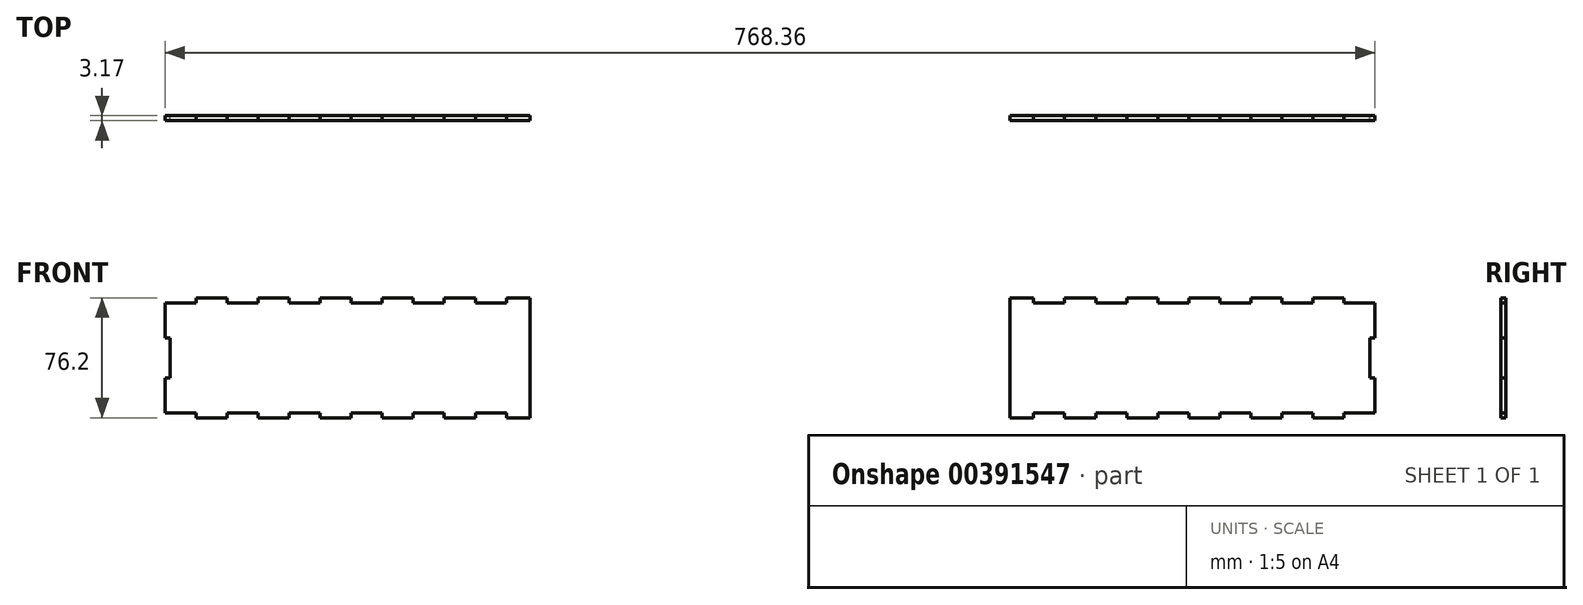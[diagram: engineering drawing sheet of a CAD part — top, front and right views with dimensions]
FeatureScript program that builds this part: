
annotation { "Feature Type Name" : "Feature", "Feature Type Description" : "" }
export const myFeature = defineFeature(function(context is Context, id is Id, definition is map)
    precondition{}
    {
        {
            var Q0;
            Q0=qCreatedBy(makeId("Front.planeOp"),FACE);
            var sketch = newSketch(context, id + "F0", { "sketchPlane" : qUnion([Q0])});
            skLineSegment(sketch, "E0.bottom", {"start": v(-384.18, -38.1) * mm, "end": v(384.17, -38.1) * mm, "construction": true});
            skLineSegment(sketch, "E0.left", {"start": v(-384.18, -38.1) * mm, "end": v(-384.18, 38.1) * mm, "construction": true});
            skPoint(sketch, "E0.middle", {"position": v(0, 0) * mm});
            skLineSegment(sketch, "E1", {"start": v(-384.18, 12.7) * mm, "end": v(-381, 12.7) * mm});
            skLineSegment(sketch, "E2", {"start": v(-381, 12.7) * mm, "end": v(-381, -12.7) * mm});
            skLineSegment(sketch, "E3", {"start": v(-381, -12.7) * mm, "end": v(-384.18, -12.7) * mm});
            skLineSegment(sketch, "E4", {"start": v(-384.18, -12.7) * mm, "end": v(-384.18, -38.1) * mm});
            skLineSegment(sketch, "E5", {"start": v(-384.18, 34.92) * mm, "end": v(-364.47, 34.92) * mm});
            skLineSegment(sketch, "E6", {"start": v(-364.47, 34.92) * mm, "end": v(-364.47, 38.1) * mm});
            skLineSegment(sketch, "E7", {"start": v(-364.47, 38.1) * mm, "end": v(-344.77, 38.1) * mm});
            skLineSegment(sketch, "E8", {"start": v(-344.77, 38.1) * mm, "end": v(-344.77, 34.93) * mm});
            skLineSegment(sketch, "E9", {"start": v(-384.18, 38.1) * mm, "end": v(384.17, 38.1) * mm, "construction": true});
            skLineSegment(sketch, "E10.1.0.0", {"start": v(-344.77, 34.92) * mm, "end": v(-325.07, 34.92) * mm});
            skLineSegment(sketch, "E10.1.0.1", {"start": v(-325.07, 34.92) * mm, "end": v(-325.07, 38.1) * mm});
            skLineSegment(sketch, "E10.1.0.2", {"start": v(-325.07, 38.1) * mm, "end": v(-305.37, 38.1) * mm});
            skLineSegment(sketch, "E10.1.0.3", {"start": v(-305.37, 38.1) * mm, "end": v(-305.37, 34.93) * mm});
            skLineSegment(sketch, "E10.2.0.0", {"start": v(-305.37, 34.92) * mm, "end": v(-285.67, 34.92) * mm});
            skLineSegment(sketch, "E10.2.0.1", {"start": v(-285.67, 34.92) * mm, "end": v(-285.67, 38.1) * mm});
            skLineSegment(sketch, "E10.2.0.2", {"start": v(-285.67, 38.1) * mm, "end": v(-265.97, 38.1) * mm});
            skLineSegment(sketch, "E10.2.0.3", {"start": v(-265.97, 38.1) * mm, "end": v(-265.97, 34.93) * mm});
            skLineSegment(sketch, "E10.3.0.0", {"start": v(-265.97, 34.92) * mm, "end": v(-246.27, 34.92) * mm});
            skLineSegment(sketch, "E10.3.0.1", {"start": v(-246.27, 34.92) * mm, "end": v(-246.27, 38.1) * mm});
            skLineSegment(sketch, "E10.3.0.2", {"start": v(-246.27, 38.1) * mm, "end": v(-226.56, 38.1) * mm});
            skLineSegment(sketch, "E10.3.0.3", {"start": v(-226.56, 38.1) * mm, "end": v(-226.56, 34.93) * mm});
            skLineSegment(sketch, "E10.4.0.0", {"start": v(-226.56, 34.92) * mm, "end": v(-206.86, 34.92) * mm});
            skLineSegment(sketch, "E10.4.0.1", {"start": v(-206.86, 34.92) * mm, "end": v(-206.86, 38.1) * mm});
            skLineSegment(sketch, "E10.4.0.2", {"start": v(-206.86, 38.1) * mm, "end": v(-187.16, 38.1) * mm});
            skLineSegment(sketch, "E10.4.0.3", {"start": v(-187.16, 38.1) * mm, "end": v(-187.16, 34.93) * mm});
            skLineSegment(sketch, "E10.5.0.0", {"start": v(-187.16, 34.92) * mm, "end": v(-167.46, 34.92) * mm});
            skLineSegment(sketch, "E10.5.0.1", {"start": v(-167.46, 34.92) * mm, "end": v(-167.46, 38.1) * mm});
            skLineSegment(sketch, "E10.5.0.2", {"start": v(-167.46, 38.1) * mm, "end": v(-147.76, 38.1) * mm});
            skLineSegment(sketch, "E10.5.0.3", {"start": v(-147.76, 38.1) * mm, "end": v(-147.76, 34.93) * mm});
            skLineSegment(sketch, "E10.6.0.0", {"start": v(-147.76, 34.92) * mm, "end": v(-128.06, 34.92) * mm});
            skLineSegment(sketch, "E10.6.0.1", {"start": v(-128.06, 34.92) * mm, "end": v(-128.06, 38.1) * mm});
            skLineSegment(sketch, "E10.6.0.2", {"start": v(-128.06, 38.1) * mm, "end": v(-108.36, 38.1) * mm});
            skLineSegment(sketch, "E10.6.0.3", {"start": v(-108.36, 38.1) * mm, "end": v(-108.36, 34.93) * mm});
            skLineSegment(sketch, "E10.7.0.0", {"start": v(-108.36, 34.92) * mm, "end": v(-88.66, 34.92) * mm});
            skLineSegment(sketch, "E10.7.0.1", {"start": v(-88.66, 34.92) * mm, "end": v(-88.66, 38.1) * mm});
            skLineSegment(sketch, "E10.7.0.2", {"start": v(-88.66, 38.1) * mm, "end": v(-68.95, 38.1) * mm});
            skLineSegment(sketch, "E10.7.0.3", {"start": v(-68.95, 38.1) * mm, "end": v(-68.95, 34.93) * mm});
            skLineSegment(sketch, "E10.8.0.0", {"start": v(-68.95, 34.92) * mm, "end": v(-49.25, 34.92) * mm});
            skLineSegment(sketch, "E10.8.0.1", {"start": v(-49.25, 34.92) * mm, "end": v(-49.25, 38.1) * mm});
            skLineSegment(sketch, "E10.8.0.2", {"start": v(-49.25, 38.1) * mm, "end": v(-29.55, 38.1) * mm});
            skLineSegment(sketch, "E10.8.0.3", {"start": v(-29.55, 38.1) * mm, "end": v(-29.55, 34.93) * mm});
            skLineSegment(sketch, "E10.9.0.0", {"start": v(-29.55, 34.92) * mm, "end": v(-9.85, 34.92) * mm});
            skLineSegment(sketch, "E10.9.0.1", {"start": v(-9.85, 34.92) * mm, "end": v(-9.85, 38.1) * mm});
            skLineSegment(sketch, "E10.9.0.2", {"start": v(-9.85, 38.1) * mm, "end": v(9.85, 38.1) * mm});
            skLineSegment(sketch, "E10.9.0.3", {"start": v(9.85, 38.1) * mm, "end": v(9.85, 34.93) * mm});
            skLineSegment(sketch, "E10.10.0.0", {"start": v(9.85, 34.92) * mm, "end": v(29.55, 34.92) * mm});
            skLineSegment(sketch, "E10.10.0.1", {"start": v(29.55, 34.92) * mm, "end": v(29.55, 38.1) * mm});
            skLineSegment(sketch, "E10.10.0.2", {"start": v(29.55, 38.1) * mm, "end": v(49.25, 38.1) * mm});
            skLineSegment(sketch, "E10.10.0.3", {"start": v(49.25, 38.1) * mm, "end": v(49.25, 34.93) * mm});
            skLineSegment(sketch, "E10.11.0.0", {"start": v(49.25, 34.92) * mm, "end": v(68.95, 34.92) * mm});
            skLineSegment(sketch, "E10.11.0.1", {"start": v(68.95, 34.92) * mm, "end": v(68.95, 38.1) * mm});
            skLineSegment(sketch, "E10.11.0.2", {"start": v(68.95, 38.1) * mm, "end": v(88.66, 38.1) * mm});
            skLineSegment(sketch, "E10.11.0.3", {"start": v(88.66, 38.1) * mm, "end": v(88.66, 34.93) * mm});
            skLineSegment(sketch, "E10.12.0.0", {"start": v(88.66, 34.92) * mm, "end": v(108.36, 34.92) * mm});
            skLineSegment(sketch, "E10.12.0.1", {"start": v(108.36, 34.92) * mm, "end": v(108.36, 38.1) * mm});
            skLineSegment(sketch, "E10.12.0.2", {"start": v(108.36, 38.1) * mm, "end": v(128.06, 38.1) * mm});
            skLineSegment(sketch, "E10.12.0.3", {"start": v(128.06, 38.1) * mm, "end": v(128.06, 34.93) * mm});
            skLineSegment(sketch, "E10.13.0.0", {"start": v(128.06, 34.92) * mm, "end": v(147.76, 34.92) * mm});
            skLineSegment(sketch, "E10.13.0.1", {"start": v(147.76, 34.92) * mm, "end": v(147.76, 38.1) * mm});
            skLineSegment(sketch, "E10.13.0.2", {"start": v(147.76, 38.1) * mm, "end": v(167.46, 38.1) * mm});
            skLineSegment(sketch, "E10.13.0.3", {"start": v(167.46, 38.1) * mm, "end": v(167.46, 34.93) * mm});
            skLineSegment(sketch, "E10.14.0.0", {"start": v(167.46, 34.92) * mm, "end": v(187.16, 34.92) * mm});
            skLineSegment(sketch, "E10.14.0.1", {"start": v(187.16, 34.92) * mm, "end": v(187.16, 38.1) * mm});
            skLineSegment(sketch, "E10.14.0.2", {"start": v(187.16, 38.1) * mm, "end": v(206.86, 38.1) * mm});
            skLineSegment(sketch, "E10.14.0.3", {"start": v(206.86, 38.1) * mm, "end": v(206.86, 34.93) * mm});
            skLineSegment(sketch, "E10.15.0.0", {"start": v(206.86, 34.92) * mm, "end": v(226.56, 34.92) * mm});
            skLineSegment(sketch, "E10.15.0.1", {"start": v(226.56, 34.92) * mm, "end": v(226.56, 38.1) * mm});
            skLineSegment(sketch, "E10.15.0.2", {"start": v(226.56, 38.1) * mm, "end": v(246.27, 38.1) * mm});
            skLineSegment(sketch, "E10.15.0.3", {"start": v(246.27, 38.1) * mm, "end": v(246.27, 34.93) * mm});
            skLineSegment(sketch, "E10.16.0.0", {"start": v(246.27, 34.92) * mm, "end": v(265.97, 34.92) * mm});
            skLineSegment(sketch, "E10.16.0.1", {"start": v(265.97, 34.92) * mm, "end": v(265.97, 38.1) * mm});
            skLineSegment(sketch, "E10.16.0.2", {"start": v(265.97, 38.1) * mm, "end": v(285.67, 38.1) * mm});
            skLineSegment(sketch, "E10.16.0.3", {"start": v(285.67, 38.1) * mm, "end": v(285.67, 34.93) * mm});
            skLineSegment(sketch, "E10.17.0.0", {"start": v(285.67, 34.92) * mm, "end": v(305.37, 34.92) * mm});
            skLineSegment(sketch, "E10.17.0.1", {"start": v(305.37, 34.92) * mm, "end": v(305.37, 38.1) * mm});
            skLineSegment(sketch, "E10.17.0.2", {"start": v(305.37, 38.1) * mm, "end": v(325.07, 38.1) * mm});
            skLineSegment(sketch, "E10.17.0.3", {"start": v(325.07, 38.1) * mm, "end": v(325.07, 34.93) * mm});
            skLineSegment(sketch, "E10.18.0.0", {"start": v(325.07, 34.92) * mm, "end": v(344.77, 34.92) * mm});
            skLineSegment(sketch, "E10.18.0.1", {"start": v(344.77, 34.92) * mm, "end": v(344.77, 38.1) * mm});
            skLineSegment(sketch, "E10.18.0.2", {"start": v(344.77, 38.1) * mm, "end": v(364.47, 38.1) * mm});
            skLineSegment(sketch, "E10.18.0.3", {"start": v(364.47, 38.1) * mm, "end": v(364.47, 34.93) * mm});
            skLineSegment(sketch, "E10.19.0.0", {"start": v(364.47, 34.92) * mm, "end": v(384.18, 34.92) * mm});
            skLineSegment(sketch, "E10.direction1", {"start": v(-384.18, 34.92) * mm, "end": v(-344.77, 34.92) * mm, "construction": true});
            skLineSegment(sketch, "E11", {"start": v(-384.18, 34.92) * mm, "end": v(-384.18, 12.7) * mm});
            skLineSegment(sketch, "E12.MirrorCS", {"start": v(-364.47, -34.92) * mm, "end": v(-364.47, -38.1) * mm});
            skLineSegment(sketch, "E13.MirrorCS", {"start": v(-265.97, -38.1) * mm, "end": v(-265.97, -34.93) * mm});
            skLineSegment(sketch, "E14.MirrorCS", {"start": v(364.47, -38.1) * mm, "end": v(364.47, -34.93) * mm});
            skLineSegment(sketch, "E15.MirrorCS", {"start": v(206.86, -38.1) * mm, "end": v(206.86, -34.93) * mm});
            skLineSegment(sketch, "E16.MirrorCS", {"start": v(49.25, -38.1) * mm, "end": v(49.25, -34.93) * mm});
            skLineSegment(sketch, "E17.MirrorCS", {"start": v(-108.36, -38.1) * mm, "end": v(-108.36, -34.93) * mm});
            skLineSegment(sketch, "E18.MirrorCS", {"start": v(-325.07, -34.92) * mm, "end": v(-325.07, -38.1) * mm});
            skLineSegment(sketch, "E19.MirrorCS", {"start": v(-344.77, -38.1) * mm, "end": v(-344.77, -34.93) * mm});
            skLineSegment(sketch, "E20.MirrorCS", {"start": v(128.06, -38.1) * mm, "end": v(128.06, -34.93) * mm});
            skLineSegment(sketch, "E21.MirrorCS", {"start": v(-29.55, -38.1) * mm, "end": v(-29.55, -34.93) * mm});
            skLineSegment(sketch, "E22.MirrorCS", {"start": v(-187.16, -38.1) * mm, "end": v(-187.16, -34.93) * mm});
            skLineSegment(sketch, "E23.MirrorCS", {"start": v(285.67, -38.1) * mm, "end": v(285.67, -34.93) * mm});
            skLineSegment(sketch, "E24.MirrorCS", {"start": v(305.37, -34.92) * mm, "end": v(305.37, -38.1) * mm});
            skLineSegment(sketch, "E25.MirrorCS", {"start": v(147.76, -34.92) * mm, "end": v(147.76, -38.1) * mm});
            skLineSegment(sketch, "E26.MirrorCS", {"start": v(-9.85, -34.92) * mm, "end": v(-9.85, -38.1) * mm});
            skLineSegment(sketch, "E27.MirrorCS", {"start": v(-167.46, -34.92) * mm, "end": v(-167.46, -38.1) * mm});
            skLineSegment(sketch, "E28.MirrorCS", {"start": v(-246.27, -34.92) * mm, "end": v(-246.27, -38.1) * mm});
            skLineSegment(sketch, "E29.MirrorCS", {"start": v(226.56, -34.92) * mm, "end": v(226.56, -38.1) * mm});
            skLineSegment(sketch, "E30.MirrorCS", {"start": v(68.95, -34.92) * mm, "end": v(68.95, -38.1) * mm});
            skLineSegment(sketch, "E31.MirrorCS", {"start": v(-88.66, -34.92) * mm, "end": v(-88.66, -38.1) * mm});
            skLineSegment(sketch, "E32.MirrorCS", {"start": v(-305.37, -38.1) * mm, "end": v(-305.37, -34.93) * mm});
            skLineSegment(sketch, "E33.MirrorCS", {"start": v(88.66, -38.1) * mm, "end": v(88.66, -34.93) * mm});
            skLineSegment(sketch, "E34.MirrorCS", {"start": v(-68.95, -38.1) * mm, "end": v(-68.95, -34.93) * mm});
            skLineSegment(sketch, "E35.MirrorCS", {"start": v(-226.56, -38.1) * mm, "end": v(-226.56, -34.93) * mm});
            skLineSegment(sketch, "E36.MirrorCS", {"start": v(246.27, -38.1) * mm, "end": v(246.27, -34.93) * mm});
            skLineSegment(sketch, "E37.MirrorCS", {"start": v(-285.67, -34.92) * mm, "end": v(-285.67, -38.1) * mm});
            skLineSegment(sketch, "E38.MirrorCS", {"start": v(344.77, -34.92) * mm, "end": v(344.77, -38.1) * mm});
            skLineSegment(sketch, "E39.MirrorCS", {"start": v(187.16, -34.92) * mm, "end": v(187.16, -38.1) * mm});
            skLineSegment(sketch, "E40.MirrorCS", {"start": v(29.55, -34.92) * mm, "end": v(29.55, -38.1) * mm});
            skLineSegment(sketch, "E41.MirrorCS", {"start": v(-128.06, -34.92) * mm, "end": v(-128.06, -38.1) * mm});
            skLineSegment(sketch, "E42.MirrorCS", {"start": v(-49.25, -34.92) * mm, "end": v(-49.25, -38.1) * mm});
            skLineSegment(sketch, "E43.MirrorCS", {"start": v(108.36, -34.92) * mm, "end": v(108.36, -38.1) * mm});
            skLineSegment(sketch, "E44.MirrorCS", {"start": v(-206.86, -34.92) * mm, "end": v(-206.86, -38.1) * mm});
            skLineSegment(sketch, "E45.MirrorCS", {"start": v(265.97, -34.92) * mm, "end": v(265.97, -38.1) * mm});
            skLineSegment(sketch, "E46.MirrorCS", {"start": v(325.07, -38.1) * mm, "end": v(325.07, -34.93) * mm});
            skLineSegment(sketch, "E47.MirrorCS", {"start": v(9.85, -38.1) * mm, "end": v(9.85, -34.93) * mm});
            skLineSegment(sketch, "E48.MirrorCS", {"start": v(167.46, -38.1) * mm, "end": v(167.46, -34.93) * mm});
            skLineSegment(sketch, "E49.MirrorCS", {"start": v(-147.76, -38.1) * mm, "end": v(-147.76, -34.93) * mm});
            skLineSegment(sketch, "E50.MirrorCS", {"start": v(108.36, -38.1) * mm, "end": v(128.06, -38.1) * mm});
            skLineSegment(sketch, "E51.MirrorCS", {"start": v(-49.25, -38.1) * mm, "end": v(-29.55, -38.1) * mm});
            skLineSegment(sketch, "E52.MirrorCS", {"start": v(-206.86, -38.1) * mm, "end": v(-187.16, -38.1) * mm});
            skLineSegment(sketch, "E53.MirrorCS", {"start": v(265.97, -38.1) * mm, "end": v(285.67, -38.1) * mm});
            skLineSegment(sketch, "E54.MirrorCS", {"start": v(-325.07, -38.1) * mm, "end": v(-305.37, -38.1) * mm});
            skLineSegment(sketch, "E55.MirrorCS", {"start": v(-384.18, -34.92) * mm, "end": v(-364.47, -34.92) * mm});
            skLineSegment(sketch, "E56.MirrorCS", {"start": v(-364.47, -38.1) * mm, "end": v(-344.77, -38.1) * mm});
            skLineSegment(sketch, "E57.MirrorCS", {"start": v(305.37, -38.1) * mm, "end": v(325.07, -38.1) * mm});
            skLineSegment(sketch, "E58.MirrorCS", {"start": v(147.76, -38.1) * mm, "end": v(167.46, -38.1) * mm});
            skLineSegment(sketch, "E59.MirrorCS", {"start": v(-9.85, -38.1) * mm, "end": v(9.85, -38.1) * mm});
            skLineSegment(sketch, "E60.MirrorCS", {"start": v(-167.46, -38.1) * mm, "end": v(-147.76, -38.1) * mm});
            skLineSegment(sketch, "E61.MirrorCS", {"start": v(-246.27, -38.1) * mm, "end": v(-226.56, -38.1) * mm});
            skLineSegment(sketch, "E62.MirrorCS", {"start": v(226.56, -38.1) * mm, "end": v(246.27, -38.1) * mm});
            skLineSegment(sketch, "E63.MirrorCS", {"start": v(68.95, -38.1) * mm, "end": v(88.66, -38.1) * mm});
            skLineSegment(sketch, "E64.MirrorCS", {"start": v(-88.66, -38.1) * mm, "end": v(-68.95, -38.1) * mm});
            skLineSegment(sketch, "E65.MirrorCS", {"start": v(-285.67, -38.1) * mm, "end": v(-265.97, -38.1) * mm});
            skLineSegment(sketch, "E66.MirrorCS", {"start": v(344.77, -38.1) * mm, "end": v(364.47, -38.1) * mm});
            skLineSegment(sketch, "E67.MirrorCS", {"start": v(187.16, -38.1) * mm, "end": v(206.86, -38.1) * mm});
            skLineSegment(sketch, "E68.MirrorCS", {"start": v(29.55, -38.1) * mm, "end": v(49.25, -38.1) * mm});
            skLineSegment(sketch, "E69.MirrorCS", {"start": v(-128.06, -38.1) * mm, "end": v(-108.36, -38.1) * mm});
            skLineSegment(sketch, "E70.MirrorCS", {"start": v(-344.77, -34.92) * mm, "end": v(-325.07, -34.92) * mm});
            skLineSegment(sketch, "E71.MirrorCS", {"start": v(-265.97, -34.92) * mm, "end": v(-246.27, -34.92) * mm});
            skLineSegment(sketch, "E72.MirrorCS", {"start": v(364.47, -34.92) * mm, "end": v(384.18, -34.92) * mm});
            skLineSegment(sketch, "E73.MirrorCS", {"start": v(206.86, -34.92) * mm, "end": v(226.56, -34.92) * mm});
            skLineSegment(sketch, "E74.MirrorCS", {"start": v(49.25, -34.92) * mm, "end": v(68.95, -34.92) * mm});
            skLineSegment(sketch, "E75.MirrorCS", {"start": v(-108.36, -34.92) * mm, "end": v(-88.66, -34.92) * mm});
            skLineSegment(sketch, "E76.MirrorCS", {"start": v(-305.37, -34.92) * mm, "end": v(-285.67, -34.92) * mm});
            skLineSegment(sketch, "E77.MirrorCS", {"start": v(325.07, -34.92) * mm, "end": v(344.77, -34.92) * mm});
            skLineSegment(sketch, "E78.MirrorCS", {"start": v(167.46, -34.92) * mm, "end": v(187.16, -34.92) * mm});
            skLineSegment(sketch, "E79.MirrorCS", {"start": v(9.85, -34.92) * mm, "end": v(29.55, -34.92) * mm});
            skLineSegment(sketch, "E80.MirrorCS", {"start": v(-147.76, -34.92) * mm, "end": v(-128.06, -34.92) * mm});
            skLineSegment(sketch, "E81.MirrorCS", {"start": v(128.06, -34.92) * mm, "end": v(147.76, -34.92) * mm});
            skLineSegment(sketch, "E82.MirrorCS", {"start": v(-29.55, -34.92) * mm, "end": v(-9.85, -34.92) * mm});
            skLineSegment(sketch, "E83.MirrorCS", {"start": v(-187.16, -34.92) * mm, "end": v(-167.46, -34.92) * mm});
            skLineSegment(sketch, "E84.MirrorCS", {"start": v(285.67, -34.92) * mm, "end": v(305.37, -34.92) * mm});
            skLineSegment(sketch, "E85.MirrorCS", {"start": v(88.66, -34.92) * mm, "end": v(108.36, -34.92) * mm});
            skLineSegment(sketch, "E86.MirrorCS", {"start": v(-68.95, -34.92) * mm, "end": v(-49.25, -34.92) * mm});
            skLineSegment(sketch, "E87.MirrorCS", {"start": v(-226.56, -34.92) * mm, "end": v(-206.86, -34.92) * mm});
            skLineSegment(sketch, "E88.MirrorCS", {"start": v(246.27, -34.92) * mm, "end": v(265.97, -34.92) * mm});
            skLineSegment(sketch, "E89.MirrorCS", {"start": v(-384.18, -34.92) * mm, "end": v(-344.77, -34.92) * mm, "construction": true});
            skLineSegment(sketch, "E90.MirrorCS", {"start": v(384.18, 12.7) * mm, "end": v(381, 12.7) * mm});
            skLineSegment(sketch, "E91.MirrorCS", {"start": v(381, -12.7) * mm, "end": v(384.18, -12.7) * mm});
            skLineSegment(sketch, "E92.MirrorCS", {"start": v(384.18, 34.92) * mm, "end": v(384.18, 12.7) * mm});
            skLineSegment(sketch, "E93.MirrorCS", {"start": v(384.18, -12.7) * mm, "end": v(384.18, -38.1) * mm});
            skLineSegment(sketch, "E94.MirrorCS", {"start": v(384.18, -38.1) * mm, "end": v(384.18, 38.1) * mm, "construction": true});
            skLineSegment(sketch, "E95.MirrorCS", {"start": v(381, 12.7) * mm, "end": v(381, -12.7) * mm});
            skLineSegment(sketch, "E96", {"start": v(-152.4, 103.96) * mm, "end": v(-152.4, -103.36) * mm, "construction": true});
            skLineSegment(sketch, "E97", {"start": v(152.4, -103.75) * mm, "end": v(152.4, 100.9) * mm, "construction": true});
            skLineSegment(sketch, "E98", {"start": v(-152.4, 38.1) * mm, "end": v(-152.4, -38.1) * mm});
            skLineSegment(sketch, "E99", {"start": v(152.4, 38.1) * mm, "end": v(152.4, -38.1) * mm});
            skSolve(sketch);
        }
        {
            var Q0;
            Q0=makeQuery(id+"F0.imprint","IMPRINT",FACE,{"disambiguationData":[TD([[makeQuery(id+"F0.imprint","IMPRINT",EDGE,{"derivedFrom":sQuery(id+"F0.wireOp",EDGE,"E1")}),1.0]])]});
            var Q1;
            {var subQ6=sQuery(id+"F0.wireOp",EDGE,"E10.13.0.3");Q1=makeQuery(id+"F0.imprint","IMPRINT",FACE,{"disambiguationData":[TD([[makeQuery(id+"F0.imprint","IMPRINT",EDGE,{"derivedFrom":subQ6}),-1.0]])]});}
            extrude(context, id + "F1", {"entities" : qUnion([Q0, Q1]), "depth" : 3.17 * mm});
        }
    });
